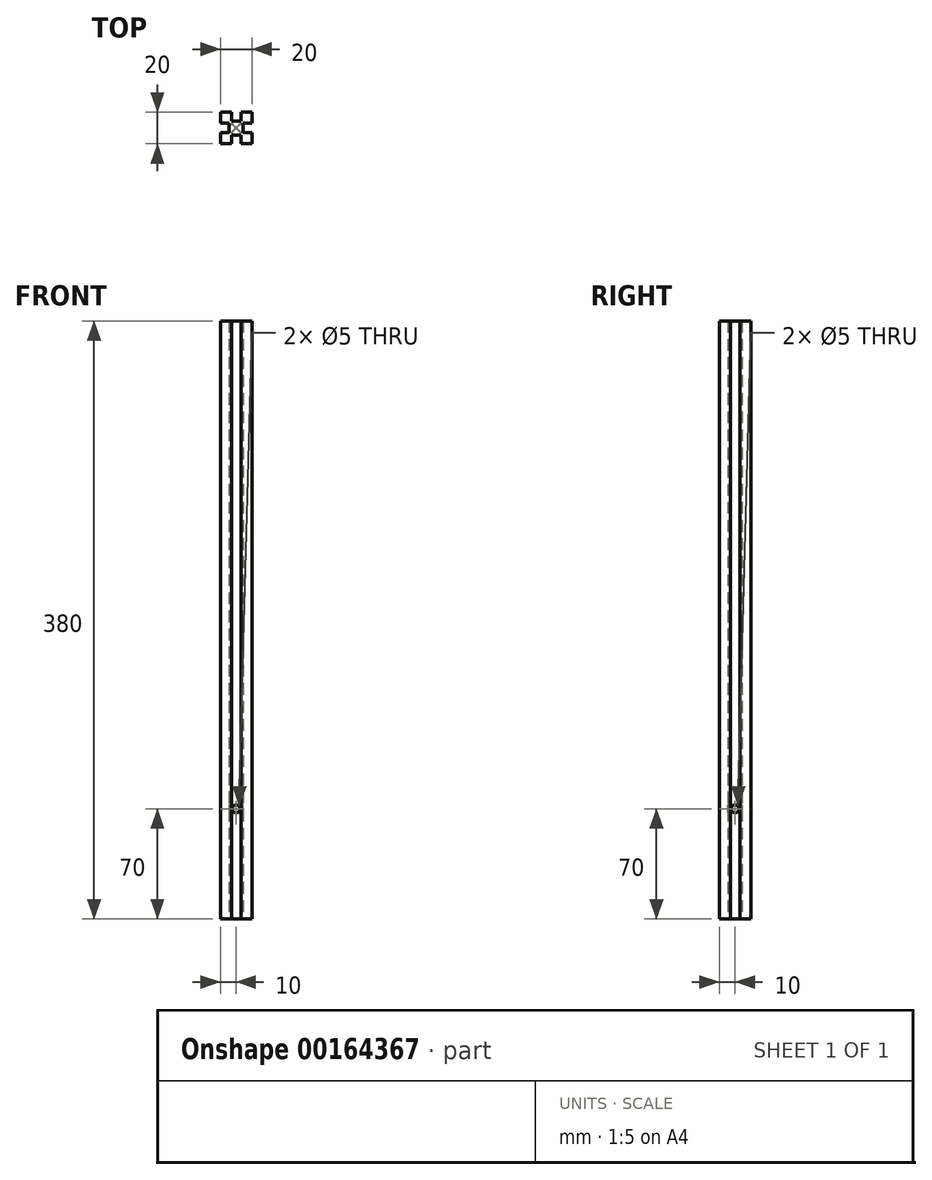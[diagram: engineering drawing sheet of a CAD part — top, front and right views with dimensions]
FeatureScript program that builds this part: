
annotation { "Feature Type Name" : "Feature", "Feature Type Description" : "" }
export const myFeature = defineFeature(function(context is Context, id is Id, definition is map)
    precondition{}
    {
        {
            var Q0;
            Q0=qCreatedBy(makeId("Top.planeOp"),FACE);
            var sketch = newSketch(context, id + "F0", { "sketchPlane" : qUnion([Q0])});
            skLineSegment(sketch, "E0.bottom", {"start": v(0, 0) * mm, "end": v(20, 0) * mm});
            skLineSegment(sketch, "E0.top", {"start": v(0, 20) * mm, "end": v(20, 20) * mm});
            skLineSegment(sketch, "E0.left", {"start": v(0, 0) * mm, "end": v(0, 20) * mm});
            skLineSegment(sketch, "E0.right", {"start": v(20, 0) * mm, "end": v(20, 20) * mm});
            skLineSegment(sketch, "E1.bottom", {"start": v(7, 20) * mm, "end": v(13, 20) * mm});
            skLineSegment(sketch, "E1.top", {"start": v(7, 14.5) * mm, "end": v(13, 14.5) * mm});
            skLineSegment(sketch, "E1.left", {"start": v(7, 20) * mm, "end": v(7, 14.5) * mm});
            skLineSegment(sketch, "E1.right", {"start": v(13, 20) * mm, "end": v(13, 14.5) * mm});
            skLineSegment(sketch, "E2.bottom", {"start": v(20, 13) * mm, "end": v(14.5, 13) * mm});
            skLineSegment(sketch, "E2.top", {"start": v(20, 7) * mm, "end": v(14.5, 7) * mm});
            skLineSegment(sketch, "E2.left", {"start": v(20, 13) * mm, "end": v(20, 7) * mm});
            skLineSegment(sketch, "E2.right", {"start": v(14.5, 13) * mm, "end": v(14.5, 7) * mm});
            skLineSegment(sketch, "E3.bottom", {"start": v(13, 0) * mm, "end": v(7, 0) * mm});
            skLineSegment(sketch, "E3.top", {"start": v(13, 5.5) * mm, "end": v(7, 5.5) * mm});
            skLineSegment(sketch, "E3.left", {"start": v(13, 0) * mm, "end": v(13, 5.5) * mm});
            skLineSegment(sketch, "E3.right", {"start": v(7, 0) * mm, "end": v(7, 5.5) * mm});
            skLineSegment(sketch, "E4.bottom", {"start": v(0, 7) * mm, "end": v(5.5, 7) * mm});
            skLineSegment(sketch, "E4.top", {"start": v(0, 13) * mm, "end": v(5.5, 13) * mm});
            skLineSegment(sketch, "E4.left", {"start": v(0, 7) * mm, "end": v(0, 13) * mm});
            skLineSegment(sketch, "E4.right", {"start": v(5.5, 7) * mm, "end": v(5.5, 13) * mm});
            skSolve(sketch);
        }
        {
            var Q0;
            Q0=makeQuery(id+"F0.imprint","IMPRINT",FACE,{"disambiguationData":[TD([[makeQuery(id+"F0.imprint","IMPRINT",EDGE,{"derivedFrom":sQuery(id+"F0.wireOp",EDGE,"E1.top")}),-1.0]])]});
            extrude(context, id + "F1", {"entities" : qUnion([Q0]), "depth" : 380 * mm});
        }
        {
            var Q0;
            Q0=makeQuery(id+"F1.opExtrude","SWEPT_FACE",FACE,{"disambiguationData":[OSD([sQuery(id+"F0.wireOp",EDGE,"E3.top")])]});
            var sketch = newSketch(context, id + "F2", { "sketchPlane" : qUnion([Q0])});
            skCircle(sketch, "E5", {"center": v(10, 70) * mm, "radius": 2.5 * mm});
            skPoint(sketch, "E5.centerSnap0", {"position": v(10, 0) * mm});
            skSolve(sketch);
        }
        {
            var Q0;
            Q0 = qSketchRegion(id + "F2", true);
            extrude(context, id + "F3", {"entities" : qUnion([Q0]), "operationType" : NewBodyOperationType.REMOVE, "oppositeDirection" : true, "depth" : 25 * mm});
        }
        {
            var Q0;
            Q0=makeQuery(id+"F1.opExtrude","SWEPT_FACE",FACE,{"disambiguationData":[OSD([sQuery(id+"F0.wireOp",EDGE,"E2.right")])]});
            var sketch = newSketch(context, id + "F4", { "sketchPlane" : qUnion([Q0])});
            skCircle(sketch, "E6", {"center": v(10, 70) * mm, "radius": 2.5 * mm});
            skPoint(sketch, "E6.centerSnap0", {"position": v(10, 0) * mm});
            skSolve(sketch);
        }
        {
            var Q0;
            Q0 = qSketchRegion(id + "F4", true);
            extrude(context, id + "F5", {"entities" : qUnion([Q0]), "operationType" : NewBodyOperationType.REMOVE, "oppositeDirection" : true, "depth" : 25 * mm});
        }
    });
